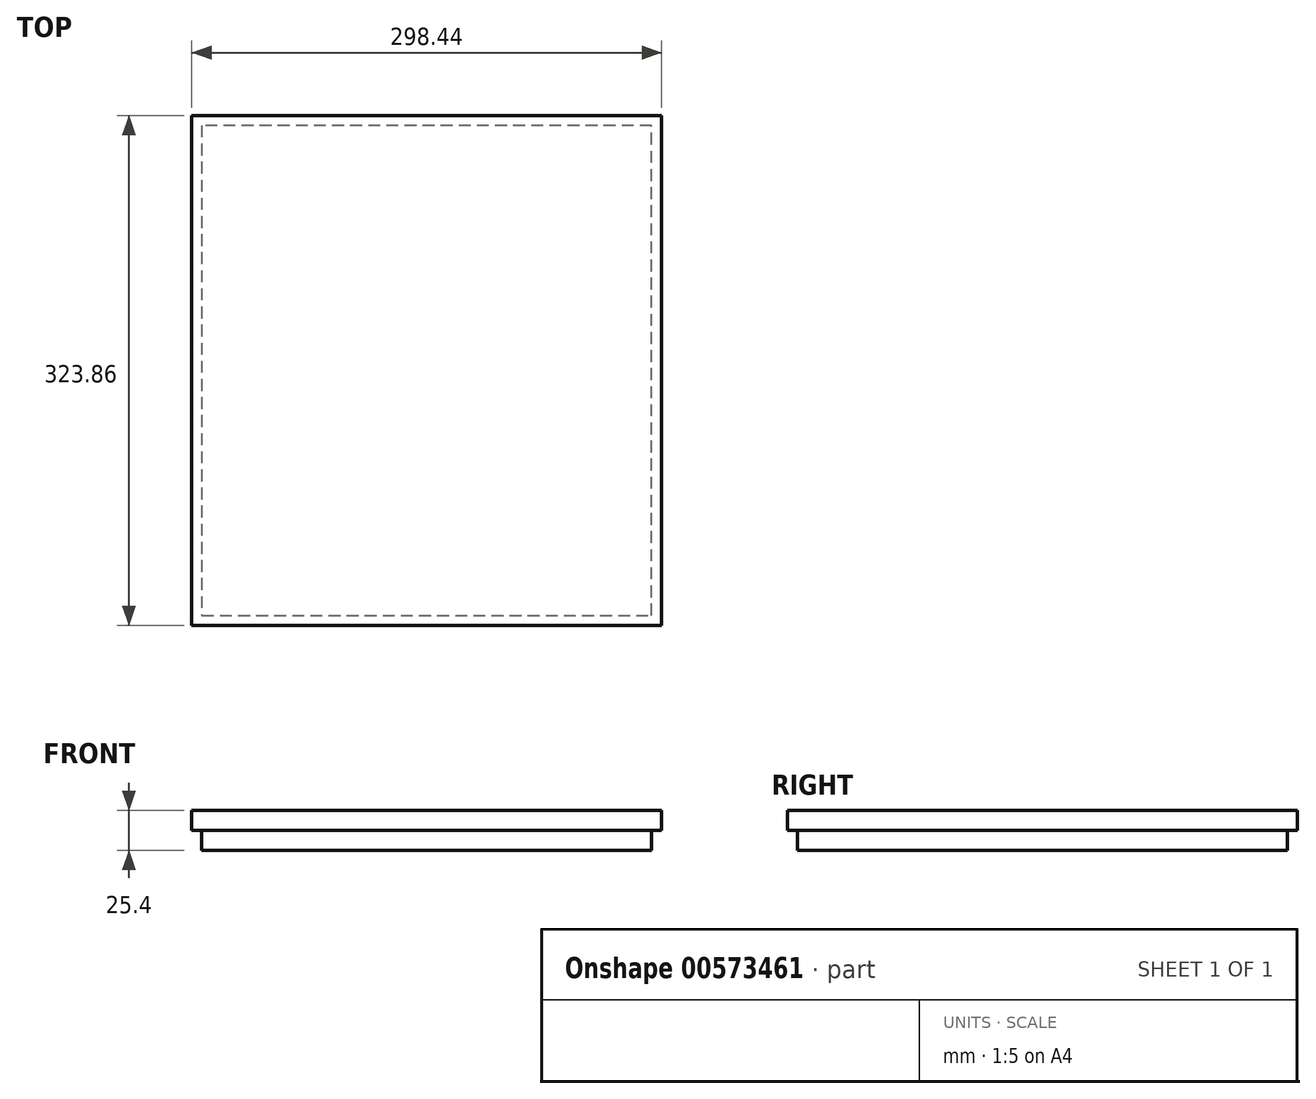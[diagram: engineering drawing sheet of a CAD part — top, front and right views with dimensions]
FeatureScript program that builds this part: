
annotation { "Feature Type Name" : "Feature", "Feature Type Description" : "" }
export const myFeature = defineFeature(function(context is Context, id is Id, definition is map)
    precondition{}
    {
        {
            var Q0;
            Q0=qCreatedBy(makeId("Top.planeOp"),FACE);
            var sketch = newSketch(context, id + "F0", { "sketchPlane" : qUnion([Q0])});
            skLineSegment(sketch, "E0.bottom", {"start": v(-142.87, -155.58) * mm, "end": v(142.88, -155.58) * mm});
            skLineSegment(sketch, "E0.top", {"start": v(-142.88, 155.58) * mm, "end": v(142.87, 155.58) * mm});
            skLineSegment(sketch, "E0.left", {"start": v(-142.87, -155.58) * mm, "end": v(-142.88, 155.58) * mm});
            skLineSegment(sketch, "E0.right", {"start": v(142.88, -155.58) * mm, "end": v(142.87, 155.58) * mm});
            skPoint(sketch, "E0.middle", {"position": v(0, 0) * mm});
            skSolve(sketch);
        }
        {
            var Q0;
            Q0 = qSketchRegion(id + "F0", true);
            extrude(context, id + "F1", {"entities" : qUnion([Q0]), "oppositeDirection" : true, "depth" : 25.4 * mm, "offsetDistance" : 25.4 * mm});
        }
        {
            var Q0;
            Q0=makeQuery(id+"F1.opExtrude","SWEPT_FACE",FACE,{"disambiguationData":[OSD([sQuery(id+"F0.wireOp",EDGE,"E0.bottom")])]});
            var sketch = newSketch(context, id + "F2", { "sketchPlane" : qUnion([Q0])});
            skLineSegment(sketch, "E1.bottom", {"start": v(-142.87, 0) * mm, "end": v(142.88, 0) * mm});
            skLineSegment(sketch, "E1.top", {"start": v(-142.87, -12.7) * mm, "end": v(142.88, -12.7) * mm});
            skLineSegment(sketch, "E1.left", {"start": v(-142.87, 0) * mm, "end": v(-142.87, -12.7) * mm});
            skLineSegment(sketch, "E1.right", {"start": v(142.88, 0) * mm, "end": v(142.88, -12.7) * mm});
            skSolve(sketch);
        }
        {
            var Q0;
            Q0=makeQuery(id+"F1.opExtrude","SWEPT_FACE",FACE,{"disambiguationData":[OSD([sQuery(id+"F0.wireOp",EDGE,"E0.top")])]});
            var sketch = newSketch(context, id + "F3", { "sketchPlane" : qUnion([Q0])});
            skLineSegment(sketch, "E2.bottom", {"start": v(-142.87, 0) * mm, "end": v(142.88, 0) * mm});
            skLineSegment(sketch, "E2.top", {"start": v(-142.87, -12.7) * mm, "end": v(142.88, -12.7) * mm});
            skLineSegment(sketch, "E2.left", {"start": v(-142.87, 0) * mm, "end": v(-142.87, -12.7) * mm});
            skLineSegment(sketch, "E2.right", {"start": v(142.88, 0) * mm, "end": v(142.88, -12.7) * mm});
            skSolve(sketch);
        }
        {
            var Q0;
            Q0=makeQuery(id+"F3.imprint","IMPRINT",FACE,{"disambiguationData":[TD([[makeQuery(id+"F3.imprint","IMPRINT",EDGE,{"derivedFrom":sQuery(id+"F3.wireOp",EDGE,"E2.bottom")}),1.0]])]});
            extrude(context, id + "F4", {"entities" : qUnion([Q0]), "operationType" : NewBodyOperationType.ADD, "depth" : 6.35 * mm, "offsetDistance" : 25.4 * mm});
        }
        {
            var Q0;
            Q0=makeQuery(id+"F2.imprint","IMPRINT",FACE,{"disambiguationData":[TD([[makeQuery(id+"F2.imprint","IMPRINT",EDGE,{"derivedFrom":sQuery(id+"F2.wireOp",EDGE,"E1.bottom")}),-1.0]])]});
            extrude(context, id + "F5", {"entities" : qUnion([Q0]), "operationType" : NewBodyOperationType.ADD, "depth" : 6.35 * mm, "offsetDistance" : 25.4 * mm});
        }
        {
            var Q0;
            Q0=makeQuery(id+"F5.boolean.opBoolean","MERGE",FACE,{"derivedFrom":[makeQuery(id+"F4.boolean.opBoolean","MERGE",FACE,{"derivedFrom":[makeQuery(id+"F1.opExtrude","SWEPT_FACE",FACE,{"disambiguationData":[OSD([sQuery(id+"F0.wireOp",EDGE,"E0.right")])]}),makeQuery(id+"F4.opExtrude","SWEPT_FACE",FACE,{"disambiguationData":[OSD([sQuery(id+"F3.wireOp",EDGE,"E2.left")])]})]}),makeQuery(id+"F5.opExtrude","SWEPT_FACE",FACE,{"disambiguationData":[OSD([sQuery(id+"F2.wireOp",EDGE,"E1.right")])]})]});
            var sketch = newSketch(context, id + "F6", { "sketchPlane" : qUnion([Q0])});
            skLineSegment(sketch, "E3.bottom", {"start": v(-161.93, 0) * mm, "end": v(161.92, 0) * mm});
            skLineSegment(sketch, "E3.top", {"start": v(-161.93, -12.7) * mm, "end": v(161.92, -12.7) * mm});
            skLineSegment(sketch, "E3.left", {"start": v(-161.93, 0) * mm, "end": v(-161.93, -12.7) * mm});
            skLineSegment(sketch, "E3.right", {"start": v(161.92, 0) * mm, "end": v(161.92, -12.7) * mm});
            skSolve(sketch);
        }
        {
            var Q0;
            Q0=makeQuery(id+"F5.boolean.opBoolean","MERGE",FACE,{"derivedFrom":[makeQuery(id+"F4.boolean.opBoolean","MERGE",FACE,{"derivedFrom":[makeQuery(id+"F1.opExtrude","SWEPT_FACE",FACE,{"disambiguationData":[OSD([sQuery(id+"F0.wireOp",EDGE,"E0.left")])]}),makeQuery(id+"F4.opExtrude","SWEPT_FACE",FACE,{"disambiguationData":[OSD([sQuery(id+"F3.wireOp",EDGE,"E2.right")])]})]}),makeQuery(id+"F5.opExtrude","SWEPT_FACE",FACE,{"disambiguationData":[OSD([sQuery(id+"F2.wireOp",EDGE,"E1.left")])]})]});
            var sketch = newSketch(context, id + "F7", { "sketchPlane" : qUnion([Q0])});
            skLineSegment(sketch, "E4.bottom", {"start": v(-161.93, 0) * mm, "end": v(161.92, 0) * mm});
            skLineSegment(sketch, "E4.top", {"start": v(-161.93, -12.7) * mm, "end": v(161.92, -12.7) * mm});
            skLineSegment(sketch, "E4.left", {"start": v(-161.93, 0) * mm, "end": v(-161.93, -12.7) * mm});
            skLineSegment(sketch, "E4.right", {"start": v(161.92, 0) * mm, "end": v(161.92, -12.7) * mm});
            skSolve(sketch);
        }
        {
            var Q0;
            Q0=makeQuery(id+"F7.imprint","IMPRINT",FACE,{"disambiguationData":[TD([[makeQuery(id+"F7.imprint","IMPRINT",EDGE,{"derivedFrom":sQuery(id+"F7.wireOp",EDGE,"E4.bottom")}),1.0]])]});
            extrude(context, id + "F8", {"entities" : qUnion([Q0]), "operationType" : NewBodyOperationType.ADD, "depth" : 6.35 * mm, "offsetDistance" : 25.4 * mm});
        }
        {
            var Q0;
            Q0=makeQuery(id+"F6.imprint","IMPRINT",FACE,{"disambiguationData":[TD([[makeQuery(id+"F6.imprint","IMPRINT",EDGE,{"derivedFrom":sQuery(id+"F6.wireOp",EDGE,"E3.bottom")}),-1.0]])]});
            extrude(context, id + "F9", {"entities" : qUnion([Q0]), "operationType" : NewBodyOperationType.ADD, "depth" : 6.35 * mm, "offsetDistance" : 25.4 * mm});
        }
    });
